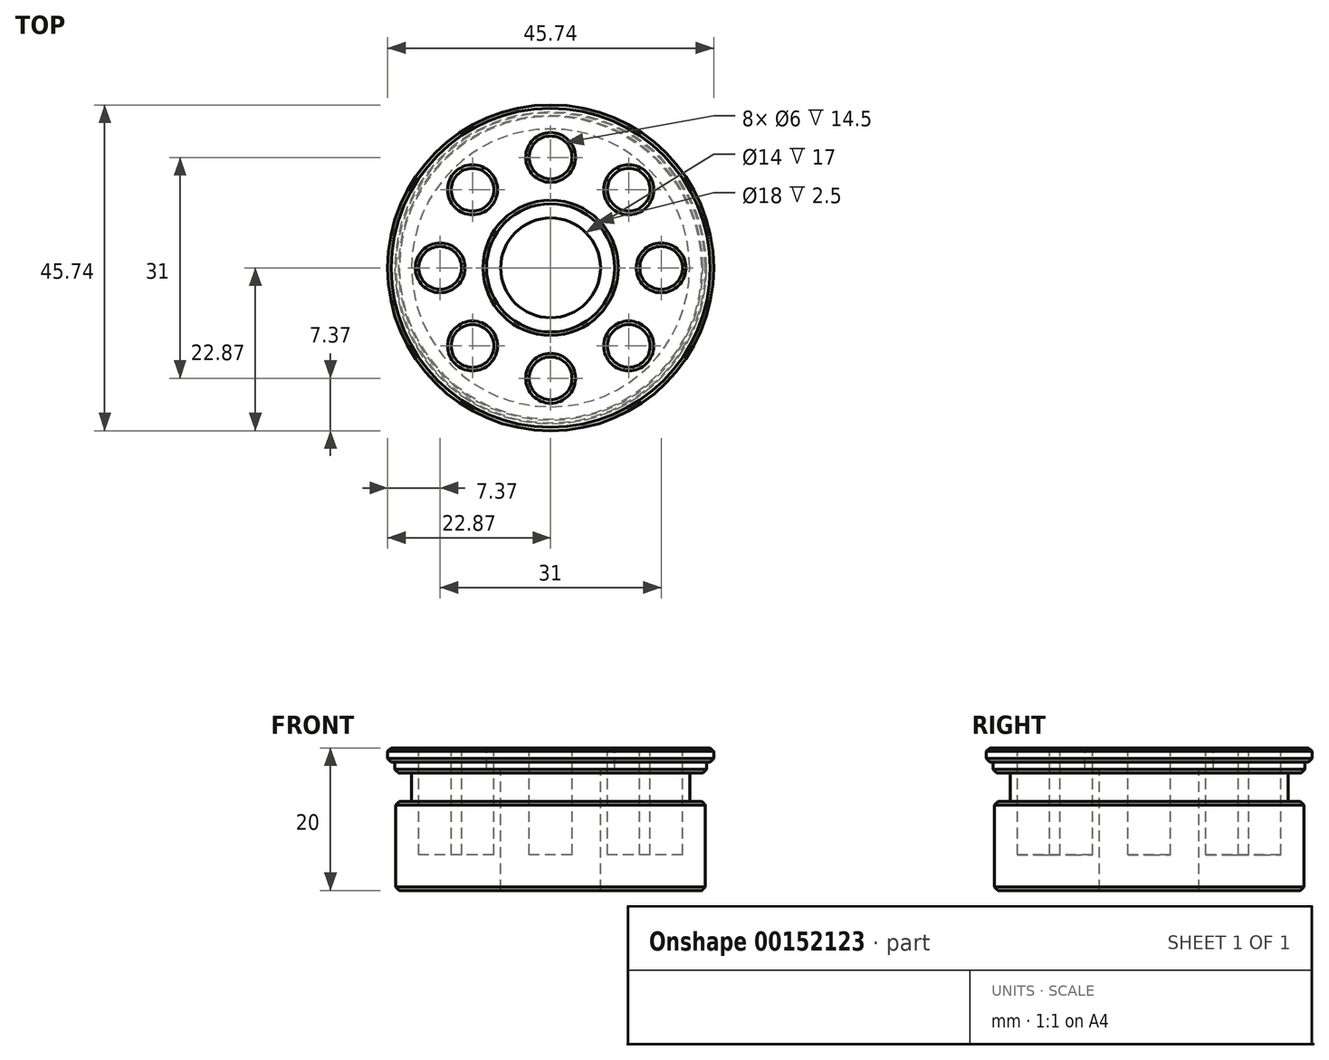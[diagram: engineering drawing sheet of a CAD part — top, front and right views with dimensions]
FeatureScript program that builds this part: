
annotation { "Feature Type Name" : "Feature", "Feature Type Description" : "" }
export const myFeature = defineFeature(function(context is Context, id is Id, definition is map)
    precondition{}
    {
        {
            var Q0;
            Q0=qCreatedBy(makeId("Front.planeOp"),FACE);
            var sketch = newSketch(context, id + "F0", { "sketchPlane" : qUnion([Q0])});
            skLineSegment(sketch, "E0", {"start": v(0, 10) * mm, "end": v(-22.87, 10) * mm});
            skLineSegment(sketch, "E1", {"start": v(0, 10) * mm, "end": v(0, -10) * mm});
            skLineSegment(sketch, "E2", {"start": v(0, -10) * mm, "end": v(-21.72, -10) * mm});
            skLineSegment(sketch, "E3", {"start": v(-22.87, 10) * mm, "end": v(-22.87, 8) * mm});
            skLineSegment(sketch, "E4", {"start": v(-22.87, 8) * mm, "end": v(-21.87, 8) * mm});
            skLineSegment(sketch, "E5", {"start": v(-21.87, 8) * mm, "end": v(-21.87, 6.5) * mm});
            skLineSegment(sketch, "E6", {"start": v(-21.87, 6.5) * mm, "end": v(-19.5, 6.5) * mm});
            skLineSegment(sketch, "E7", {"start": v(-19.5, 6.5) * mm, "end": v(0, 6.5) * mm, "construction": true});
            skLineSegment(sketch, "E8", {"start": v(-19.5, 6.5) * mm, "end": v(-19.5, 2.5) * mm});
            skLineSegment(sketch, "E9", {"start": v(-21.72, -10) * mm, "end": v(-21.72, 2.5) * mm});
            skLineSegment(sketch, "E10", {"start": v(-19.5, 2.5) * mm, "end": v(-21.72, 2.5) * mm});
            skSolve(sketch);
        }
        {
            var Q0;
            Q0=makeQuery(id+"F0.imprint","IMPRINT",FACE,{"disambiguationData":[TD([[makeQuery(id+"F0.imprint","IMPRINT",EDGE,{"derivedFrom":sQuery(id+"F0.wireOp",EDGE,"E0")}),1.0]])]});
            var Q1;
            Q1=sQuery(id+"F0.wireOp",EDGE,"E1");
            revolve(context, id + "F1", {"entities" : qUnion([Q0]), "axis" : qUnion([Q1]), "revolveType" : RevolveType.FULL});
        }
        {
            var Q0;
            Q0=makeQuery(id+"F1.opRevolve","SWEPT_FACE",FACE,{"disambiguationData":[OSD([sQuery(id+"F0.wireOp",EDGE,"E0")])]});
            var sketch = newSketch(context, id + "F2", { "sketchPlane" : qUnion([Q0])});
            skCircle(sketch, "E11", {"center": v(0, 0) * mm, "radius": 7 * mm});
            skLineSegment(sketch, "E12", {"start": v(0, 0) * mm, "end": v(0, 15.5) * mm, "construction": true});
            skCircle(sketch, "E13", {"center": v(0, 15.5) * mm, "radius": 3 * mm});
            skCircle(sketch, "E14.1.0", {"center": v(-10.96, 10.96) * mm, "radius": 3 * mm});
            skCircle(sketch, "E14.2.0", {"center": v(-15.5, 0) * mm, "radius": 3 * mm});
            skCircle(sketch, "E14.3.0", {"center": v(-10.96, -10.96) * mm, "radius": 3 * mm});
            skCircle(sketch, "E14.4.0", {"center": v(0, -15.5) * mm, "radius": 3 * mm});
            skCircle(sketch, "E14.5.0", {"center": v(10.96, -10.96) * mm, "radius": 3 * mm});
            skCircle(sketch, "E14.6.0", {"center": v(15.5, 0) * mm, "radius": 3 * mm});
            skCircle(sketch, "E14.7.0", {"center": v(10.96, 10.96) * mm, "radius": 3 * mm});
            skCircle(sketch, "E15", {"center": v(0, 0) * mm, "radius": 9 * mm});
            skSolve(sketch);
        }
        {
            var Q0;
            Q0=makeQuery(id+"F2.imprint","IMPRINT",FACE,{"disambiguationData":[TD([[makeQuery(id+"F2.imprint","IMPRINT",EDGE,{"derivedFrom":sQuery(id+"F2.wireOp",EDGE,"E11")}),1.0]])]});
            extrude(context, id + "F3", {"entities" : qUnion([Q0]), "operationType" : NewBodyOperationType.REMOVE, "endBound" : BoundingType.THROUGH_ALL, "oppositeDirection" : true, "depth" : 25 * mm});
        }
        {
            var Q0;
            Q0=makeQuery(id+"F2.imprint","IMPRINT",FACE,{"disambiguationData":[TD([[makeQuery(id+"F2.imprint","IMPRINT",EDGE,{"derivedFrom":sQuery(id+"F2.wireOp",EDGE,"E14.1.0")}),1.0]])]});
            var Q1;
            Q1=makeQuery(id+"F2.imprint","IMPRINT",FACE,{"disambiguationData":[TD([[makeQuery(id+"F2.imprint","IMPRINT",EDGE,{"derivedFrom":sQuery(id+"F2.wireOp",EDGE,"E14.7.0")}),1.0]])]});
            var Q2;
            Q2=makeQuery(id+"F2.imprint","IMPRINT",FACE,{"disambiguationData":[TD([[makeQuery(id+"F2.imprint","IMPRINT",EDGE,{"derivedFrom":sQuery(id+"F2.wireOp",EDGE,"E14.6.0")}),1.0]])]});
            var Q3;
            Q3=makeQuery(id+"F2.imprint","IMPRINT",FACE,{"disambiguationData":[TD([[makeQuery(id+"F2.imprint","IMPRINT",EDGE,{"derivedFrom":sQuery(id+"F2.wireOp",EDGE,"E14.5.0")}),1.0]])]});
            var Q4;
            Q4=makeQuery(id+"F2.imprint","IMPRINT",FACE,{"disambiguationData":[TD([[makeQuery(id+"F2.imprint","IMPRINT",EDGE,{"derivedFrom":sQuery(id+"F2.wireOp",EDGE,"E14.4.0")}),1.0]])]});
            var Q5;
            Q5=makeQuery(id+"F2.imprint","IMPRINT",FACE,{"disambiguationData":[TD([[makeQuery(id+"F2.imprint","IMPRINT",EDGE,{"derivedFrom":sQuery(id+"F2.wireOp",EDGE,"E14.3.0")}),1.0]])]});
            var Q6;
            Q6=makeQuery(id+"F2.imprint","IMPRINT",FACE,{"disambiguationData":[TD([[makeQuery(id+"F2.imprint","IMPRINT",EDGE,{"derivedFrom":sQuery(id+"F2.wireOp",EDGE,"E14.2.0")}),1.0]])]});
            var Q7;
            Q7=makeQuery(id+"F2.imprint","IMPRINT",FACE,{"disambiguationData":[TD([[makeQuery(id+"F2.imprint","IMPRINT",EDGE,{"derivedFrom":sQuery(id+"F2.wireOp",EDGE,"E13")}),1.0]])]});
            extrude(context, id + "F4", {"entities" : qUnion([Q0, Q1, Q2, Q3, Q4, Q5, Q6, Q7]), "operationType" : NewBodyOperationType.REMOVE, "oppositeDirection" : true, "depth" : 15 * mm});
        }
        {
            var Q0;
            Q0=makeQuery(id+"F2.imprint","IMPRINT",FACE,{"disambiguationData":[TD([[makeQuery(id+"F2.imprint","IMPRINT",EDGE,{"derivedFrom":sQuery(id+"F2.wireOp",EDGE,"E11")}),-1.0]])]});
            extrude(context, id + "F5", {"entities" : qUnion([Q0]), "operationType" : NewBodyOperationType.REMOVE, "oppositeDirection" : true, "depth" : 3 * mm});
        }
        {
            var Q0;
            Q0=makeQuery(id+"F1.opRevolve","SWEPT_FACE",FACE,{"disambiguationData":[OSD([sQuery(id+"F0.wireOp",EDGE,"E0")])]});
            chamfer(context, id + "F6", {"entities" : qUnion([Q0]), "width" : .5 * mm, "tangentPropagation" : true});
        }
        {
            var Q0;
            Q0=makeQuery(id+"F1.opRevolve","SWEPT_EDGE",EDGE,{"disambiguationData":[OSD([sQuery(id+"F0.wireOp",EDGE,"E3"),sQuery(id+"F0.wireOp",EDGE,"E4")])]});
            var Q1;
            Q1=makeQuery(id+"F1.opRevolve","SWEPT_EDGE",EDGE,{"disambiguationData":[OSD([sQuery(id+"F0.wireOp",EDGE,"E5"),sQuery(id+"F0.wireOp",EDGE,"E6")])]});
            var Q2;
            Q2=makeQuery(id+"F1.opRevolve","SWEPT_EDGE",EDGE,{"disambiguationData":[OSD([sQuery(id+"F0.wireOp",EDGE,"E9"),sQuery(id+"F0.wireOp",EDGE,"E10")])]});
            var Q3;
            Q3=makeQuery(id+"F1.opRevolve","SWEPT_EDGE",EDGE,{"disambiguationData":[OSD([sQuery(id+"F0.wireOp",EDGE,"E2"),sQuery(id+"F0.wireOp",EDGE,"E9")])]});
            chamfer(context, id + "F7", {"entities" : qUnion([Q0, Q1, Q2, Q3]), "width" : .5 * mm, "tangentPropagation" : true});
        }
    });
